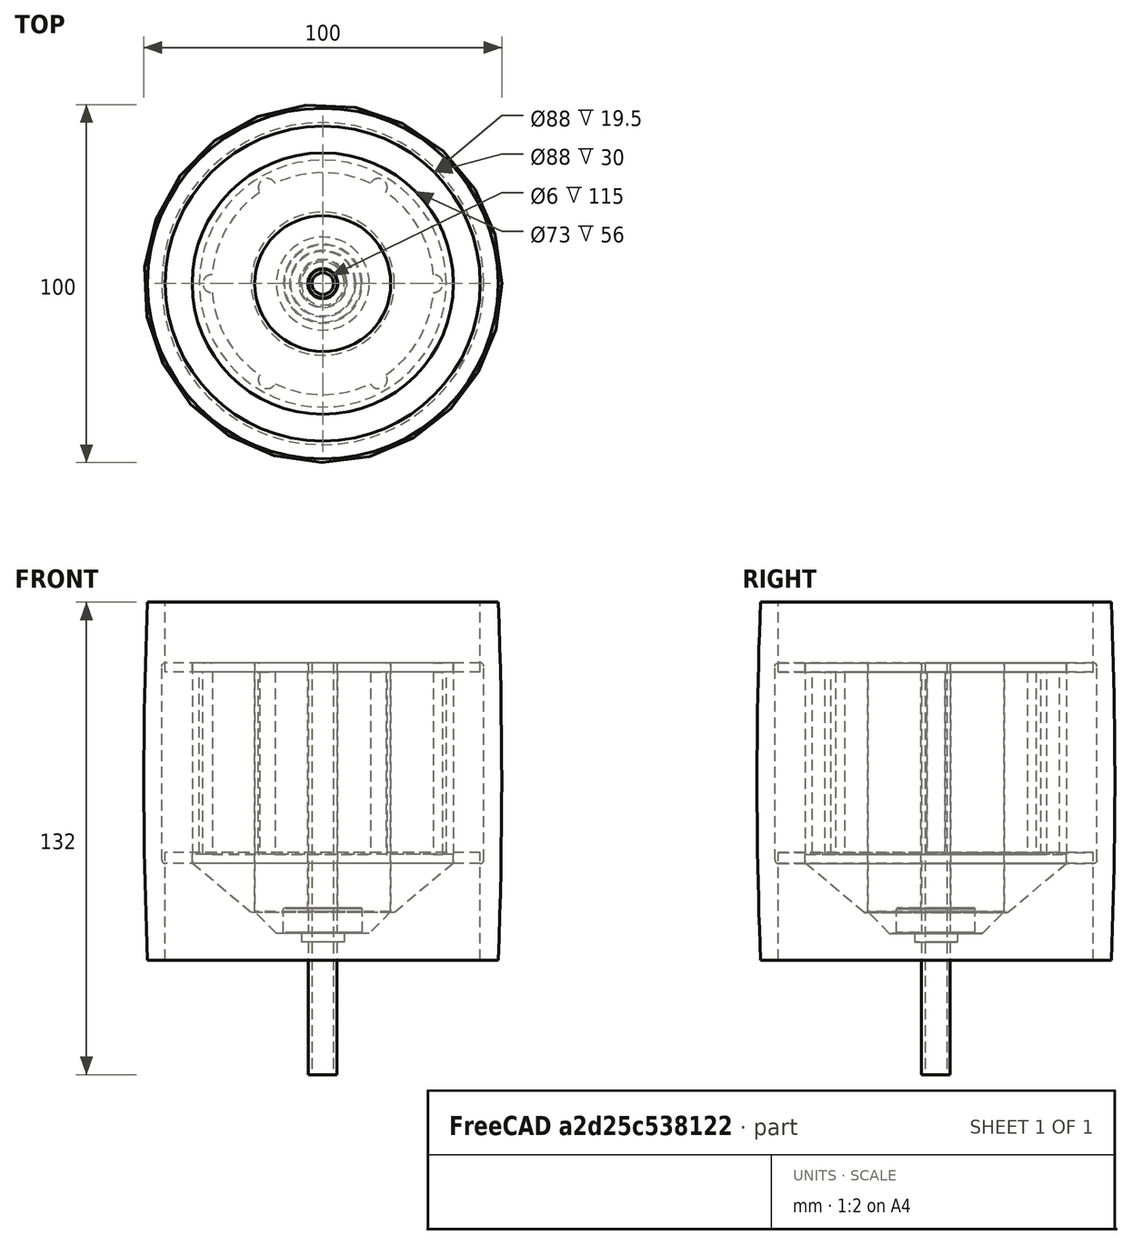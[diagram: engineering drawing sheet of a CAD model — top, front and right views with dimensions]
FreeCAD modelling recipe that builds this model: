
FCSTD DOCUMENT  (FreeCAD 0.22R37898 (Git))
Label: hub with skateboard motor
License: All rights reserved
LicenseURL: http://en.wikipedia.org/wiki/All_rights_reserved
objects: Part::Feature×5, Sketcher::SketchObject×1, App::Part×1, PartDesign::Revolution×1, PartDesign::Body×1
note: 9 computed .brp shape members not serialized (recipe doc carries the construction recipe); baked Part::Feature solids carry a one-line shape summary decoded from their .brp

FEATURE [Sketcher::SketchObject] Sketch
  AttachmentSupport = -> [XZ_Plane001]
  FullyConstrained = false
  MapMode = 5
  Placement = pos=(0,0,0) rot=(1,0,0;1.5708rad)
  sketch-geometry (9):
    g0: ArcOfCircle CenterX=-1200.5 CenterY=42.5 CenterZ=0 NormalX=0 NormalY=0 NormalZ=1 AngleXU=0 Radius=1250.5 StartAngle=6.24319 EndAngle=6.32318
    g1: LineSegment StartX=49 StartY=-7.5 StartZ=0 EndX=44 EndY=-7.5 EndZ=0
    g2: LineSegment StartX=44 StartY=-7.5 StartZ=0 EndX=44 EndY=22.5 EndZ=0
    g3: LineSegment StartX=44 StartY=22.5 StartZ=0 EndX=34.5 EndY=22.5 EndZ=0
    g4: LineSegment StartX=34.5 StartY=22.5 StartZ=0 EndX=34.5 EndY=73 EndZ=0
    g5: LineSegment StartX=34.5 StartY=73 StartZ=0 EndX=44 EndY=73 EndZ=0
    g6: LineSegment StartX=44 StartY=73 StartZ=0 EndX=44 EndY=92.5 EndZ=0
    g7: LineSegment StartX=50 StartY=42.5 StartZ=0 EndX=-1200.5 EndY=42.5 EndZ=0
    g8: LineSegment StartX=49 StartY=92.5 StartZ=0 EndX=44 EndY=92.5 EndZ=0
  constraints (27):
    c: Coincident(g0,g1)
    c: Horizontal(g1)
    c: Coincident(g1,g2)
    c: Coincident(g2,g3)
    c: Coincident(g3,g4)
    c: Vertical(g4)
    c: Vertical(g2)
    c: Horizontal(g3)
    c: DistanceY(g-1,g3) = 22.5
    c: DistanceY(g2,g2) = 30
    c: DistanceY(g0,g0) = 100
    c: DistanceY(g4,g4) = 50.5
    c: Coincident(g5,g4)
    c: Horizontal(g5)
    c: Coincident(g6,g5)
    c: Vertical(g6)
    c: Perpendicular(g7,g0) = 4.71239
    c: Coincident(g8,g0)
    c: Coincident(g8,g6)
    c: Horizontal(g8)
    c: DistanceX(g-1,g7) = 50
    c: Vertical(g0,g0)
    c: DistanceX(g0,g7) = 1
    c: Coincident(g7,g0)
    c: Equal(g5,g3)
    c: DistanceX(g-1,g3) = 34.5
    c: DistanceX(g1,g1) = 5
FEATURE [Part::Feature] Part__Feature  label="Axis"
  shape: bbox 12 x 12 x 115 mm, 8 faces (baked)
FEATURE [Part::Feature] Part__Feature001  label="Stator"
  shape: bbox 38 x 38 x 75.5 mm, 7 faces (baked)
FEATURE [Part::Feature] Part__Feature002  label="Outer"
  shape: bbox 73 x 73 x 69.69 mm, 26 faces (baked)
FEATURE [Part::Feature] Part__Feature003  label="Wheel"
  shape: bbox 97.42 x 97.42 x 56 mm, 6 faces (baked)
FEATURE [Part::Feature] Part__Feature004  label="Bearing"
  Placement = pos=(0,0,3.5) rot=(0,0,1;0rad)
  shape: bbox 22 x 22 x 7 mm, 14 faces (baked)
FEATURE [App::Part] skateboard_motor
  Group = -> [Part__Feature,Part__Feature001,Part__Feature002,Part__Feature003,Part__Feature004]
  Origin = -> Origin
FEATURE [PartDesign::Revolution] Revolution
  Angle = 360
  Angle2 = 60
  Axis = (0,2e-16,1)
  Base = (0,0,0)
  Placement = pos=(0,0,0) rot=(1,0,0;1.5708rad)
  Profile = -> Sketch
  ReferenceAxis = -> Sketch [V_Axis]
  Reversed = true
  Suppressed = false
  Type = 0
FEATURE [PartDesign::Body] Body  label="Corpo"
  AllowCompound = false
  Group = -> [Sketch,Revolution]
  Origin = -> Origin001
  Tip = -> Revolution
